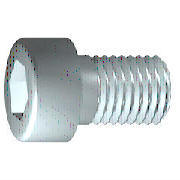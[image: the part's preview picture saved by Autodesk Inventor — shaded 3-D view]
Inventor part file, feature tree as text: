
AUTODESK INVENTOR PART (.ipt)
format: ipt  version: 2013 (Build 170138000, 138)  size: 172,544 bytes
history: native  units: mm (DEFAULTED — no unit token found)
features: sketch x2, extrude x1, plane x1, fillet x1
ambient origin geometry x7: Origin, YZ Plane, XY Plane, X Axis, Y Axis, Z Axis, Center Point
bodies: Solid1 (feature_tree), Body (feature_tree)
feature tree (5):
  extrude  "Slot"  Depth=0.766912mm
  plane  "Work Plane1"
  fillet  "Fillet2"  Radius=8.0mm
  sketch  "Sketch1"  dims[d1=28.0mm d2=0.766912mm d3=8.0mm]
  sketch  "Sketch2"  dims[d4=4.0mm d5=60.0deg d6=8.0mm d7=8.0mm d8=6.928203mm d9=13.0mm d10=90.0deg d11=10.0mm d12=0.0mm d13=28.0mm d14=0.0mm d15=0.766812mm d16=0.766813mm d17=0.8mm d19=0.0mm d26=200.0mm d27=45.0deg d28=0.0mm d29=0.0mm d30=0.1mm]
